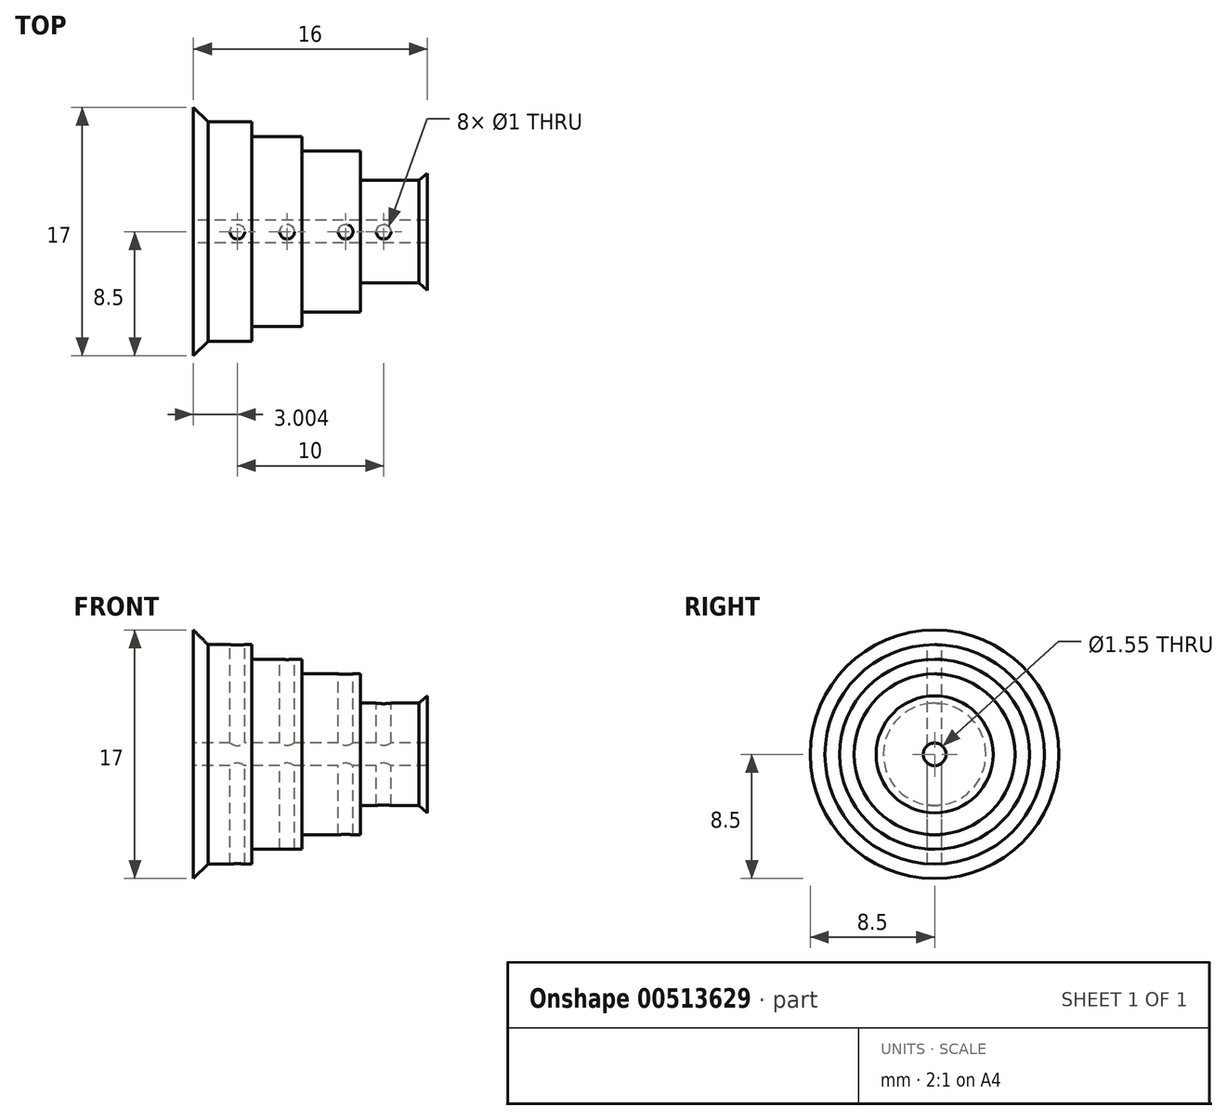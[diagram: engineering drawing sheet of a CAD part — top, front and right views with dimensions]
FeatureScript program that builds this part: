
annotation { "Feature Type Name" : "Feature", "Feature Type Description" : "" }
export const myFeature = defineFeature(function(context is Context, id is Id, definition is map)
    precondition{}
    {
        {
            var Q0;
            Q0=qCreatedBy(makeId("Front.planeOp"),FACE);
            var sketch = newSketch(context, id + "F0", { "sketchPlane" : qUnion([Q0])});
            skLineSegment(sketch, "E0", {"start": v(-22.67, 0) * mm, "end": v(34.76, 0) * mm, "construction": true});
            skLineSegment(sketch, "E1", {"start": v(0, 8.5) * mm, "end": v(0, 0) * mm});
            skLineSegment(sketch, "E2", {"start": v(0, 0) * mm, "end": v(0, 8.5) * mm});
            skLineSegment(sketch, "E3", {"start": v(16, 4) * mm, "end": v(16, 0) * mm});
            skLineSegment(sketch, "E4", {"start": v(0, 0.78) * mm, "end": v(16, 0.78) * mm});
            skLineSegment(sketch, "E5", {"start": v(15.4, 3.5) * mm, "end": v(16, 4) * mm});
            skLineSegment(sketch, "E6", {"start": v(16, 4) * mm, "end": v(16, 4) * mm});
            skLineSegment(sketch, "E7", {"start": v(1, 7.5) * mm, "end": v(4, 7.5) * mm});
            skLineSegment(sketch, "E8", {"start": v(11.4, 3.5) * mm, "end": v(15.4, 3.5) * mm});
            skLineSegment(sketch, "E9", {"start": v(1, 7.5) * mm, "end": v(0, 8.5) * mm});
            skLineSegment(sketch, "E10", {"start": v(4, 7.5) * mm, "end": v(4, 6.5) * mm});
            skLineSegment(sketch, "E11", {"start": v(4, 6.5) * mm, "end": v(7.4, 6.5) * mm});
            skLineSegment(sketch, "E12", {"start": v(7.4, 6.5) * mm, "end": v(7.4, 5.5) * mm});
            skLineSegment(sketch, "E13", {"start": v(7.4, 5.5) * mm, "end": v(11.4, 5.5) * mm});
            skLineSegment(sketch, "E14", {"start": v(11.4, 5.5) * mm, "end": v(11.4, 3.5) * mm});
            skSolve(sketch);
        }
        {
            var Q0;
            Q0=qSketchRegion(id+"F0",true);
            var Q1;
            Q1=sQuery(id+"F0.wireOp",EDGE,"E0");
            revolve(context, id + "F1", {"entities" : qUnion([Q0]), "axis" : qUnion([Q1]), "revolveType" : RevolveType.FULL});
        }
        {
            var Q0;
            Q0=qCreatedBy(makeId("Top.planeOp"),FACE);
            var sketch = newSketch(context, id + "F2", { "sketchPlane" : qUnion([Q0])});
            skCircle(sketch, "E15", {"center": v(3, 0) * mm, "radius": 0.5 * mm});
            skCircle(sketch, "E16", {"center": v(6.4, 0) * mm, "radius": 0.5 * mm});
            skCircle(sketch, "E17", {"center": v(10.4, 0) * mm, "radius": 0.5 * mm});
            skCircle(sketch, "E18", {"center": v(13, 0) * mm, "radius": 0.5 * mm});
            skSolve(sketch);
        }
        {
            var Q0;
            Q0=qSketchRegion(id+"F2",true);
            extrude(context, id + "F3", {"entities" : qUnion([Q0]), "operationType" : NewBodyOperationType.REMOVE, "endBound" : BoundingType.SYMMETRIC, "oppositeDirection" : true, "depth" : 25 * mm, "offsetDistance" : 25 * mm});
        }
    });
